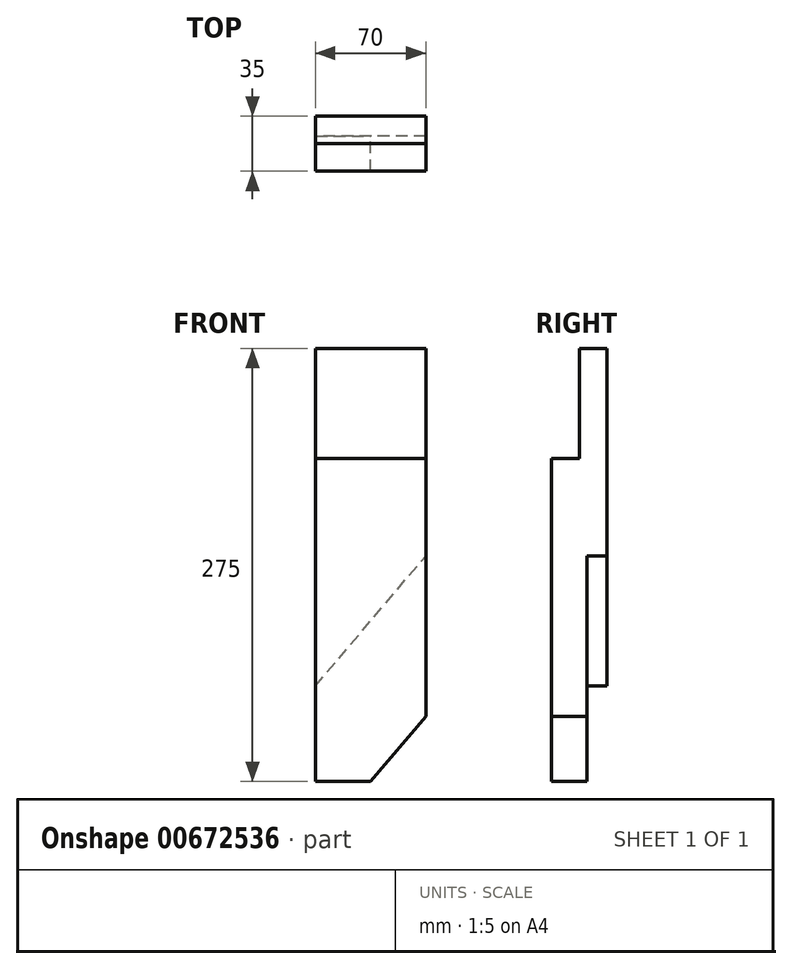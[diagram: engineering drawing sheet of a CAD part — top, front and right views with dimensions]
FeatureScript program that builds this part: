
annotation { "Feature Type Name" : "Feature", "Feature Type Description" : "" }
export const myFeature = defineFeature(function(context is Context, id is Id, definition is map)
    precondition{}
    {
        {
            var Q0;
            Q0=qCreatedBy(makeId("Front.planeOp"),FACE);
            var sketch = newSketch(context, id + "F0", { "sketchPlane" : qUnion([Q0])});
            skLineSegment(sketch, "E0.bottom", {"start": v(0, 0) * mm, "end": v(70, 0) * mm});
            skLineSegment(sketch, "E0.top", {"start": v(0, 275) * mm, "end": v(70, 275) * mm});
            skLineSegment(sketch, "E0.left", {"start": v(0, 0) * mm, "end": v(0, 275) * mm});
            skLineSegment(sketch, "E0.right", {"start": v(70, 0) * mm, "end": v(70, 275) * mm});
            skSolve(sketch);
        }
        {
            var Q0;
            Q0=makeQuery(id+"F0.imprint","IMPRINT",FACE,{"disambiguationData":[TD([[makeQuery(id+"F0.imprint","IMPRINT",EDGE,{"derivedFrom":sQuery(id+"F0.wireOp",EDGE,"E0.bottom")}),1.0]])]});
            extrude(context, id + "F1", {"entities" : qUnion([Q0]), "depth" : 35 * mm, "offsetDistance" : 25 * mm});
        }
        {
            var Q0;
            Q0=makeQuery(id+"F1.opExtrude","SWEPT_FACE",FACE,{"disambiguationData":[OSD([sQuery(id+"F0.wireOp",EDGE,"E0.right")])]});
            var sketch = newSketch(context, id + "F2", { "sketchPlane" : qUnion([Q0])});
            skLineSegment(sketch, "E1", {"start": v(-35, 205) * mm, "end": v(-17.5, 205) * mm});
            skLineSegment(sketch, "E2", {"start": v(-17.5, 205) * mm, "end": v(-17.5, 275) * mm});
            skSolve(sketch);
        }
        {
            var Q0;
            {var subQ0=sQuery(id+"F2.wireOp",EDGE,"E1");Q0=makeQuery(id+"F2.imprint","IMPRINT",FACE,{"disambiguationData":[TD([[makeQuery(id+"F2.imprint","IMPRINT",EDGE,{"derivedFrom":subQ0}),1.0]])]});}
            extrude(context, id + "F3", {"entities" : qUnion([Q0]), "operationType" : NewBodyOperationType.REMOVE, "endBound" : BoundingType.THROUGH_ALL, "oppositeDirection" : true, "depth" : 25 * mm, "offsetDistance" : 25 * mm});
        }
        {
            var Q0;
            Q0=makeQuery(id+"F1.opExtrude","CAP_FACE",FACE,{"disambiguationData":[OSD([sQuery(id+"F0.wireOp",EDGE,"E0.bottom"),sQuery(id+"F0.wireOp",EDGE,"E0.top"),sQuery(id+"F0.wireOp",EDGE,"E0.left"),sQuery(id+"F0.wireOp",EDGE,"E0.right")])],"isStart":true});
            var sketch = newSketch(context, id + "F4", { "sketchPlane" : qUnion([Q0])});
            skLineSegment(sketch, "E3", {"start": v(-70, 41.29) * mm, "end": v(-35, 0) * mm});
            skLineSegment(sketch, "E4", {"start": v(-70, 143.2) * mm, "end": v(0, 60.62) * mm});
            skSolve(sketch);
        }
        {
            var Q0;
            {var subQ3=sQuery(id+"F4.wireOp",EDGE,"E3");Q0=makeQuery(id+"F4.imprint","IMPRINT",FACE,{"disambiguationData":[TD([[makeQuery(id+"F4.imprint","IMPRINT",EDGE,{"derivedFrom":subQ3}),1.0]])]});}
            extrude(context, id + "F5", {"entities" : qUnion([Q0]), "operationType" : NewBodyOperationType.REMOVE, "oppositeDirection" : true, "depth" : 25 * mm, "offsetDistance" : 25 * mm, "symmetric" : true});
        }
        {
            var Q0;
            {var subQ0=sQuery(id+"F0.wireOp",EDGE,"E0.bottom");var subQ1=sQuery(id+"F0.wireOp",EDGE,"E0.right");Q0=makeQuery(id+"F5.boolean.opBoolean","SPLIT",FACE,{"disambiguationData":[TD([makeQuery(id+"F1.opExtrude","SWEPT_FACE",FACE,{"disambiguationData":[OSD([subQ0])]})])],"derivedFrom":makeQuery(id+"F1.opExtrude","CAP_FACE",FACE,{"disambiguationData":[OSD([subQ0,sQuery(id+"F0.wireOp",EDGE,"E0.top"),sQuery(id+"F0.wireOp",EDGE,"E0.left"),subQ1])],"isStart":true})});}
            extrude(context, id + "F6", {"entities" : qUnion([Q0]), "operationType" : NewBodyOperationType.REMOVE, "endBound" : BoundingType.THROUGH_ALL, "oppositeDirection" : true, "depth" : 25 * mm, "offsetDistance" : 25 * mm});
        }
    });
